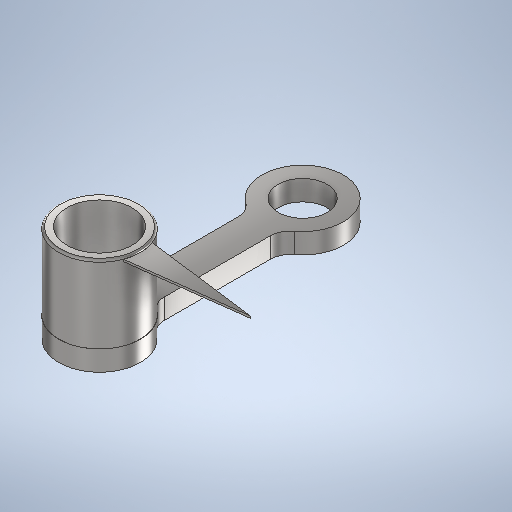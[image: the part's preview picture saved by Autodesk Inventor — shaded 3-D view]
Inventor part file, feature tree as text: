
AUTODESK INVENTOR PART (.ipt)
format: ipt  version: 2025.1 (Build 291241000, 241)  size: 325,120 bytes
history: native  units: mm
features: sketch x4, extrude x3, fillet x2, hole x1, plane x1, other x1
ambient origin geometry x8: Origin, YZ Plane, XZ Plane, XY Plane, X Axis, Y Axis, Z Axis, Center Point
bodies: Solid1 (feature_tree)
feature tree (12):
  extrude  "Extrusion1"  Depth=8.0mm
  fillet  "Fillet1"  Radius=4.0mm
  extrude  "Extrusion2"  Depth=10.0mm
  hole  "Hole1"  [1 undecoded]
  fillet  "Fillet2"  Radius=5.0mm
  plane  "Work Plane1"
  extrude  "Extrusion3"  Depth=19.0mm TaperAngle=0.0deg
  sketch  "Sketch1"  dims[d0=50.0mm d1=8.0mm d2=4.0mm]
  sketch  "Sketch2"  dims[d3=10.0mm d4=10.0mm]
  sketch  "Sketch3"  dims[d5=12.0mm d6=8.0mm d7=5.0mm d8=0.0mm]
  sketch  "Sketch5"  dims[d9=5.0mm d10=19.0mm d11=0.0mm d12=16.0mm d13=6.0mm d14=4.0mm d15=2.0mm d16=90.0deg d17=12.5mm d18=0.0mm d19=0.5mm d20=18.0mm d21=0.5mm d22=0.0mm]
  other  "Needle2"
note: 1 required parameter value undecoded (feature->parameter linkage not recoverable at this tier; creation-order binding heuristic only, values carry confidence <= 0.55)
